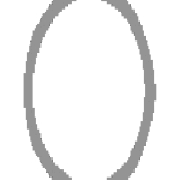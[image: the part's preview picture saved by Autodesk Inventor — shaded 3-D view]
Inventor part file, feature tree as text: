
AUTODESK INVENTOR PART (.ipt)
format: ipt  version: 2021 (Build 250183000, 183)  size: 112,128 bytes
history: native  units: in
note: dims shown in document units (in); Inventor stores cm internally (conversion verified against a paired STEP export)
features: other x4, sketch x3, plane x1
ambient origin geometry x8: Origin, YZ Plane, XZ Plane, XY Plane, X Axis, Y Axis, Z Axis, Center Point
bodies: Solid1 (feature_tree), Body (feature_tree)
feature tree (8):
  other  "Driven Length"
  other  "Frame Generator"
  other  "Start Plane"
  other  "End Plane"
  sketch  "Sketch"  dims[d2=13.2634in d4=-0.0in d5=13.2634in d6=0.12in d7=0.0in d8=90.0deg d9=13.2634in]
  sketch  "Sketch2"  dims[d0=1.0in]
  plane  "Work Plane3"
  sketch  "Sketch3"  dims[d1=0.065in]
